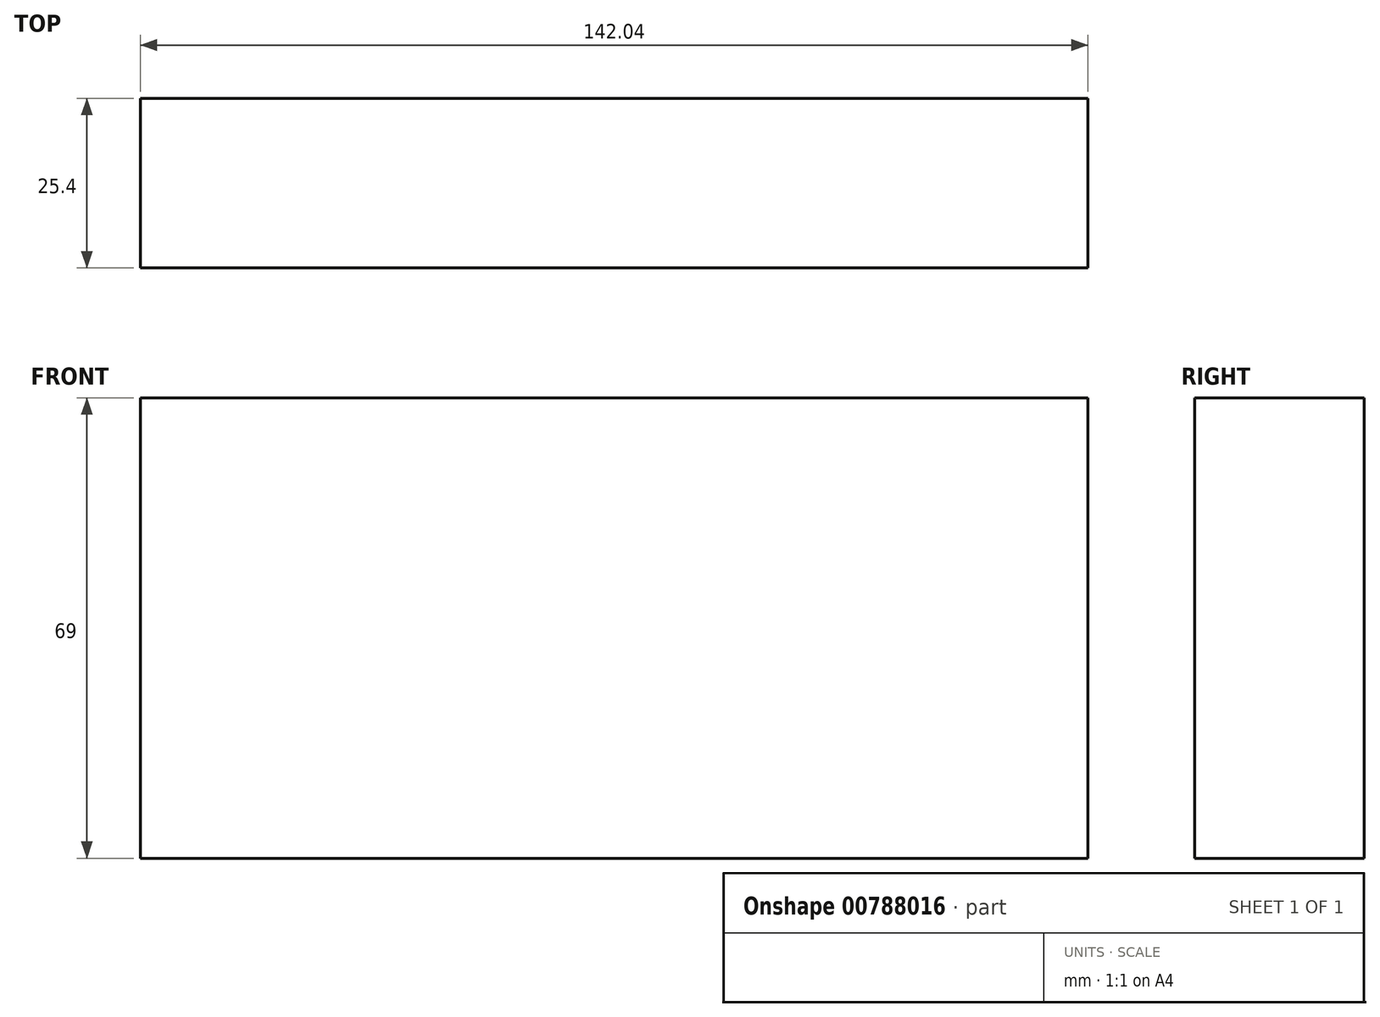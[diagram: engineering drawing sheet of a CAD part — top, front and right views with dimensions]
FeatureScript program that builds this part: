
annotation { "Feature Type Name" : "Feature", "Feature Type Description" : "" }
export const myFeature = defineFeature(function(context is Context, id is Id, definition is map)
    precondition{}
    {
        {
            var Q0;
            Q0=qCreatedBy(makeId("Front.planeOp"),FACE);
            var sketch = newSketch(context, id + "F0", { "sketchPlane" : qUnion([Q0])});
            skLineSegment(sketch, "E0.bottom", {"start": v(71.02, 34.5) * mm, "end": v(-71.02, 34.5) * mm});
            skLineSegment(sketch, "E0.top", {"start": v(71.02, -34.5) * mm, "end": v(-71.02, -34.5) * mm});
            skLineSegment(sketch, "E0.left", {"start": v(71.02, 34.5) * mm, "end": v(71.02, -34.5) * mm});
            skLineSegment(sketch, "E0.right", {"start": v(-71.02, 34.5) * mm, "end": v(-71.02, -34.5) * mm});
            skPoint(sketch, "E0.middle", {"position": v(0, 0) * mm});
            skSolve(sketch);
        }
        {
            var Q0;
            Q0 = qSketchRegion(id + "F0", true);
            extrude(context, id + "F1", {"entities" : qUnion([Q0]), "depth" : 25.4 * mm, "offsetDistance" : 25.4 * mm});
        }
    });
